# Revit family: Hand-Shower-Set_Traditional_Guinevere_TS970F2_TOTO
name_source: partatom
category: Plumbing Fixtures
revit_build: Autodesk Revit Architecture 2013 (Build: 20130531_2115(x64)
units: mm (PartAtom-declared; Revit-internal decimal feet)

## types (1)
- TS970F2
    04 CSI = 22 41 39
    95 CSI = 15416
    Assembly Code = D2010710
    CAD Drawing URL = http://assets.totousa.com
    CW Connection = No
    CWFU = 0
    Color Availability = #CP Polished Chrome, #RB Oil Rubbed Bronze
    Default Elevation = 4' - 0"
    Depth = 0' - 5 3/16"
    Description = Handshower Set
    Distance from Center of Hand Shower Holder to Connection = 0' - 2 13/32"
    Finish = Metal - TOTO - Chrome - Polished
    Flexible Hose Main Length = 2' - 1 25/32"
    Flow Rate = 3.000 GPM
    HW Connection = No
    HWFU = 0
    Height = 1' - 0 1/16"
    Manufacturer = TOTO USA, Inc.
    Manufacturer Fax = (770) 282-0002
    Model = TS970F2
    Series = Guinevere
    Shipping Weight = 4.30 lb
    Spec Sheet URL = http://assets.totousa.com
    Style = Traditional
    Subcategory = Showers
    TW Connector = Yes
    Tempered Water Connection NPT = 1"
    Tempered Water Connector = Tempered Water Connection
    Toto BIM Number = BM-00216
    URL = http://www.totousa.com
    Vent Connection = No
    WFU = 0
    Warranty = Lifetime Limited Warranty (Residential Use); One Year (Oil Rubbed Bronze); One Year Limited (Commercial Use)
    Warranty URL = http://www.totousa.com
    Waste Connection = No
    Width = 0' - 6 13/16"

## geometry (parser evidence)
native form markers: Blend x12, Sweep x3
no freeform markers — native parametric forms only
